# Revit family: Comfort_Window_H_Top_Hung_Standard
name_source: partatom
category: Windows
revit_build: Autodesk Revit 2014 (Build: 20130308_1515(x64)
units: mm (PartAtom-declared; Revit-internal decimal feet)

## types (4) — shared parameters
DG Gasket Thickness = 12 mm  [stored 0.0393701 ft]
Description = Comfort Window, Top Hung, Type H
Double Glazing Gasket Finish = Double Glazing Gasket Material
Frame Depth = 33 mm
Frame Edge Thickness = 26 mm
Limit Fixed Pane Height Max = 1800 mm
Limit Fixed Pane Height Min = 200 mm
Limit Fixed Pane Width Max = 1800 mm
Limit Fixed Pane Width Min = 200 mm
Limit Sash Height Max = 1200 mm
Limit Sash Height Min = 300 mm  [stored 0.984252 ft]
Limit Sash Width Max = 1200 mm
Limit Sash Width Min = 300 mm  [stored 0.984252 ft]
Limit Window Width Max = 1275 mm
Limit Window Width Min = 375 mm
Manufacturer = Crealco
Max System DG One Piece Thickness = 4 mm  [stored 0.0131234 ft]
Max System DG Unit Thickness = 20 mm  [stored 0.0656168 ft]
Model = Comfort Window
Rough Height = 1647 mm
Rough Width = 2226 mm
Sash Frame Gap = 5 mm  [stored 0.0164042 ft]
Sash Frame Side Gap = 12 mm  [stored 0.0393701 ft]
Sash Side Gap = 38 mm
Set Sash Height = 515 mm
Transom Height = 27 mm
URL = http://www.crealco.co.za
zero-valued in all types: Visual Light Transmittance

## per-type parameters (varying)
| type | Clearvue SHGC Value | Clearvue U Value | Energy Advantage SHGC Value | Energy Advantage U Value | Intruderprufe LowE SHGC Value | Intruderprufe LowE U Value | Intruderprufe SHGC Value | Intruderprufe U Value | SmartGlass Elite SHGC Value | SmartGlass Elite U Value | SmartGlass Plus SHGC Value | SmartGlass Plus U Value | SmartGlass Standard SHGC Value | SmartGlass Standard U Value | SmartGlass Superior SHGC Value | SmartGlass Superior U Value | Window Height | Window Width |
| Comfort-0615DT | 0.507 | 6.15 | 0.456 | 4.99 | 0.434 | 4.87 | 0.484 | 6.06 | 0.254 | 3.87 | 0.342 | 3.98 | 0.455 | 4.41 | 0.22 | 3.87 | 1490 mm  [stored 4.88845 ft] | 590 mm  [stored 1.9357 ft] |
| Comfort-0618DT | 0.542 | 6.12 | 0.487 | 4.86 | 0.462 | 4.74 | 0.517 | 6.02 | 0.269 | 3.64 | 0.363 | 3.77 | 0.485 | 4.24 | 0.235 | 3.65 | 1790 mm | 590 mm  [stored 1.9357 ft] |
| Comfort-0915DT | 0.557 | 6.11 | 0.5 | 4.81 | 0.474 | 4.69 | 0.53 | 6.02 | 0.275 | 3.57 | 0.373 | 3.7 | 0.498 | 4.18 | 0.241 | 3.57 | 1490 mm  [stored 4.88845 ft] | 890 mm |
| Comfort-0918DT | 0.592 | 6.09 | 0.531 | 4.68 | 0.502 | 4.56 | 0.562 | 5.99 | 0.29 | 3.34 | 0.394 | 3.49 | 0.527 | 4.01 | 0.253 | 3.35 | 1790 mm | 890 mm |

note: [stored X ft] marks values corroborated as IEEE doubles in the binary element streams (Revit-internal decimal feet)

## geometry (parser evidence)
native form markers: Sweep x23
no freeform markers — native parametric forms only
